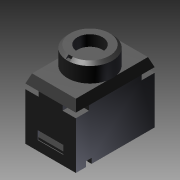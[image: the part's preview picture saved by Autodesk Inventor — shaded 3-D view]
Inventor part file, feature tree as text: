
AUTODESK INVENTOR PART (.ipt)
format: ipt  version: 2011 SP1 (Build 150282100, 282)  size: 196,096 bytes
history: native  units: in
note: dims shown in document units (in); Inventor stores cm internally (conversion verified against a paired STEP export)
features: other x28, sketch x10, extrude x9, revolve x1
ambient origin geometry x8: Origin, YZ Plane, XZ Plane, XY Plane, X Axis, Y Axis, Z Axis, Center Point
bodies: Solid1 (feature_tree)
feature tree (48):
  extrude  "Extrusion1"  Depth=0.276in TaperAngle=0.0deg
  extrude  "Extrusion2"  Depth=0.017in TaperAngle=0.0deg
  extrude  "Extrusion3"  Depth=0.018in TaperAngle=0.0deg
  extrude  "Extrusion4"  Depth=0.01in TaperAngle=0.0deg
  revolve  "Revolution1"  [1 undecoded]
  extrude  "Extrusion5"  [1 undecoded]
  extrude  "Extrusion6"  [1 undecoded]
  extrude  "Extrusion7"  [1 undecoded]
  extrude  "Extrusion8"  [1 undecoded]
  extrude  "Extrusion9"  [1 undecoded]
  other  "to_actuator_XY"
  other  "to_actuator_YZ"
  other  "to_actuator_ZX"
  other  "to_actuator_X"
  other  "to_actuator_Y"
  other  "to_actuator_Z"
  other  "to_actuator_Center"
  other  "to_dummy_XY"
  other  "to_dummy_YZ"
  other  "to_dummy_ZX"
  other  "to_dummy_X"
  other  "to_dummy_Y"
  other  "to_dummy_Z"
  other  "to_dummy_Center"
  other  "to_trmnl_hold_XY"
  other  "to_trmnl_hold_YZ"
  other  "to_trmnl_hold_ZX"
  other  "to_trmnl_hold_X"
  other  "to_trmnl_hold_Y"
  other  "to_trmnl_hold_Z"
  other  "to_trmnl_hold_Center"
  other  "to_trmnls_XY"
  other  "to_trmnls_YZ"
  other  "to_trmnls_ZX"
  other  "to_trmnls_X"
  other  "to_trmnls_Y"
  other  "to_trmnls_Z"
  other  "to_trmnls_Center"
  sketch  "Sketch_1"  dims[d0=0.213in d1=0.0in d2=0.276in d3=0.0in]
  sketch  "Sketch_2"  dims[d4=0.177in d5=0.0in d6=0.017in d7=0.0in]
  sketch  "Sketch_3"  dims[d8=360.0deg d9=0.018in d10=0.0in]
  sketch  "Sketch_4"  dims[d11=0.002in d12=0.0in d13=0.01in d14=0.0in]
  sketch  "Sketch_5"  dims[d15=0.6in d16=0.0in d17=0.09in d18=0.0in]
  sketch  "Sketch_6"
  sketch  "Sketch_7"
  sketch  "Sketch_11"
  sketch  "Sketch_13"
  sketch  "Sketch_14"
note: 6 required parameter values undecoded (feature->parameter linkage not recoverable at this tier; creation-order binding heuristic only, values carry confidence <= 0.55)